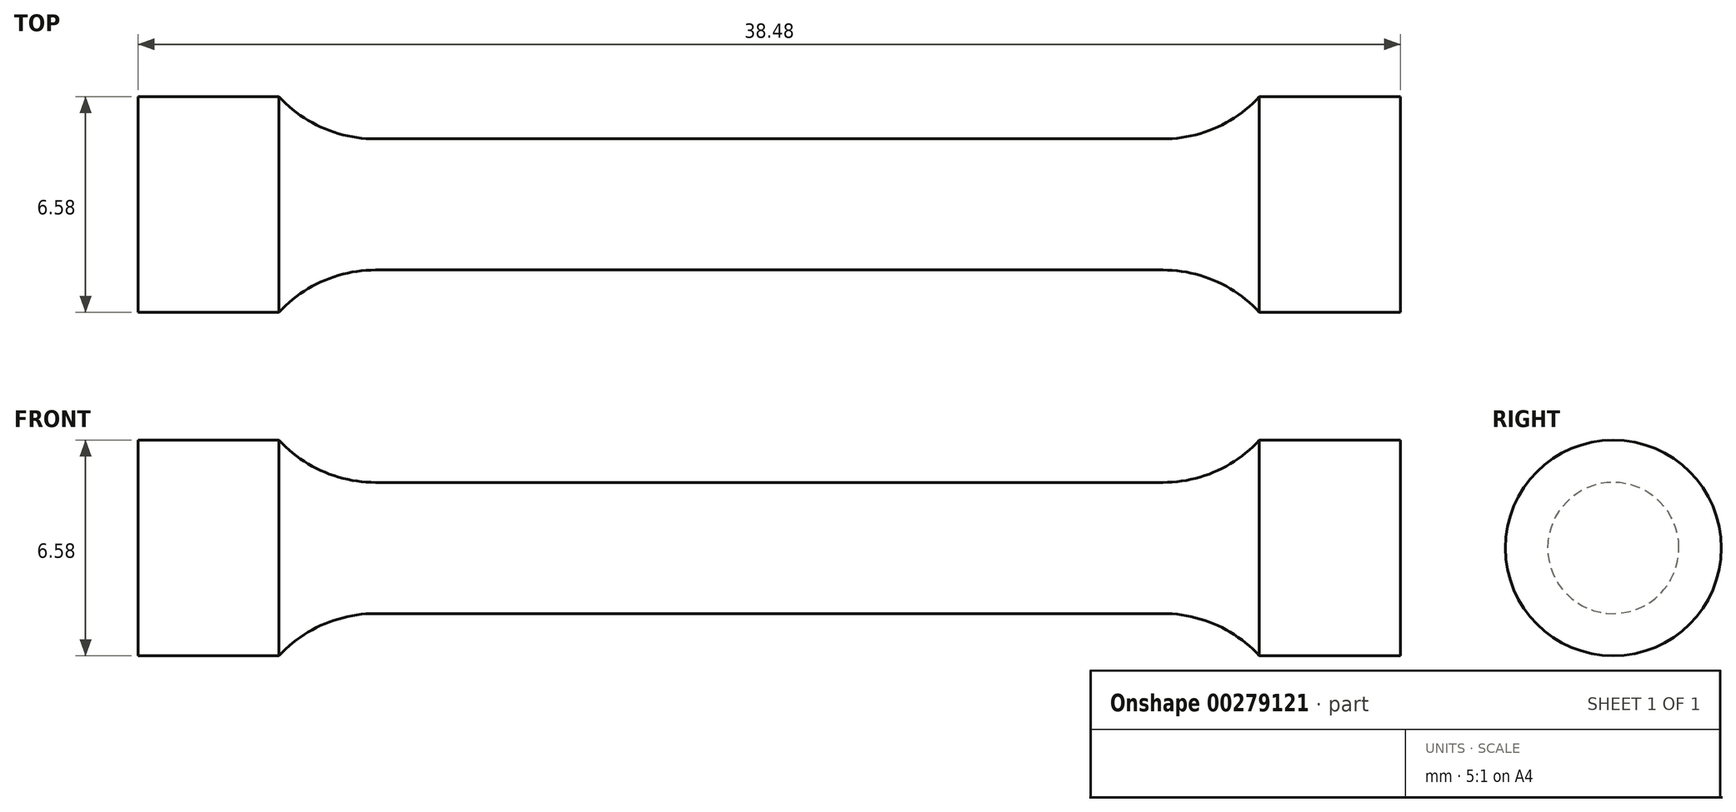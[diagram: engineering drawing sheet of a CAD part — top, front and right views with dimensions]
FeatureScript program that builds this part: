
annotation { "Feature Type Name" : "Feature", "Feature Type Description" : "" }
export const myFeature = defineFeature(function(context is Context, id is Id, definition is map)
    precondition{}
    {
        {
            var Q0;
            Q0=qCreatedBy(makeId("Front.planeOp"),FACE);
            var sketch = newSketch(context, id + "F0", { "sketchPlane" : qUnion([Q0])});
            skLineSegment(sketch, "E0", {"start": v(0, 2) * mm, "end": v(12, 2) * mm});
            skArc(sketch, "E1", {"start": v(12, 2) * mm, "mid": v(13.6, 2.34) * mm, "end": v(14.94, 3.29) * mm});
            skLineSegment(sketch, "E2", {"start": v(14.94, 3.29) * mm, "end": v(19.24, 3.29) * mm});
            skLineSegment(sketch, "E3", {"start": v(19.24, 3.29) * mm, "end": v(19.24, 0) * mm});
            skLineSegment(sketch, "E4", {"start": v(19.24, 0) * mm, "end": v(0, 0) * mm});
            skLineSegment(sketch, "E5.MirrorCS", {"start": v(0, 2) * mm, "end": v(-12, 2) * mm});
            skLineSegment(sketch, "E6.MirrorCS", {"start": v(-19.24, 0) * mm, "end": v(0, 0) * mm});
            skLineSegment(sketch, "E7.MirrorCS", {"start": v(-14.94, 3.29) * mm, "end": v(-19.24, 3.29) * mm});
            skLineSegment(sketch, "E8.MirrorCS", {"start": v(-19.24, 3.29) * mm, "end": v(-19.24, 0) * mm});
            skArc(sketch, "E9.MirrorCS", {"start": v(-12, 2) * mm, "mid": v(-13.6, 2.34) * mm, "end": v(-14.94, 3.29) * mm});
            skSolve(sketch);
        }
        {
            var Q0;
            Q0 = qSketchRegion(id + "F0", true);
            var Q1;
            Q1=sQuery(id+"F0.wireOp",EDGE,"E6.MirrorCS");
            revolve(context, id + "F1", {"entities" : qUnion([Q0]), "axis" : qUnion([Q1]), "revolveType" : RevolveType.FULL});
        }
    });
